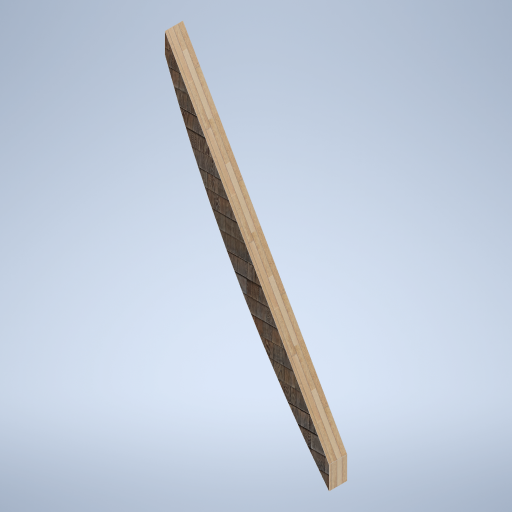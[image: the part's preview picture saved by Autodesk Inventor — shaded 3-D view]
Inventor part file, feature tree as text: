
AUTODESK INVENTOR PART (.ipt)
format: ipt  version: 2024.2 (Build 282272000, 272)  size: 302,592 bytes
history: native  units: mm
features: extrude x1, sketch x1
ambient origin geometry x8: Origin, YZ Plane, XZ Plane, XY Plane, X Axis, Y Axis, Z Axis, Center Point
bodies: Body1 (feature_tree)
feature tree (2):
  extrude  "Extrusion2"  Depth=200.0mm TaperAngle=0.0deg
  sketch  "Sketch1"  dims[d3=12000.0mm d4=200.0mm d5=0.0mm]
